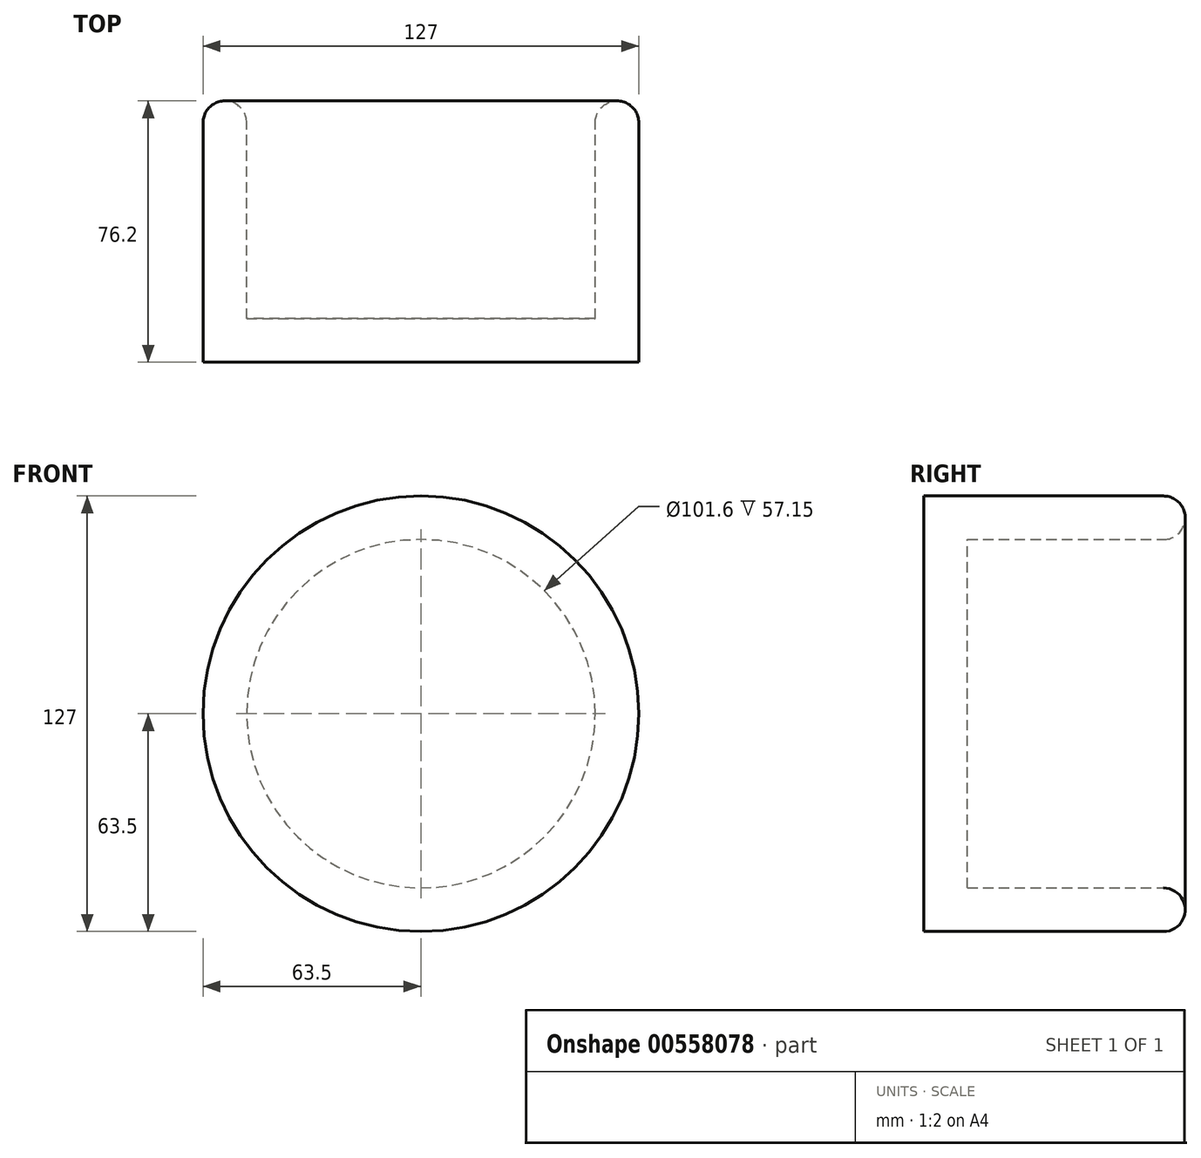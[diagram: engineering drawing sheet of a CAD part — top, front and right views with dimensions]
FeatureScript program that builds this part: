
annotation { "Feature Type Name" : "Feature", "Feature Type Description" : "" }
export const myFeature = defineFeature(function(context is Context, id is Id, definition is map)
    precondition{}
    {
        {
            var Q0;
            Q0=qCreatedBy(makeId("Front.planeOp"),FACE);
            var sketch = newSketch(context, id + "F0", { "sketchPlane" : qUnion([Q0])});
            skCircle(sketch, "E0", {"center": v(0, 0) * mm, "radius": 63.5 * mm});
            skSolve(sketch);
        }
        {
            var Q0;
            Q0=makeQuery(id+"F0.imprint","IMPRINT",FACE,{"disambiguationData":[TD([[makeQuery(id+"F0.imprint","IMPRINT",EDGE,{"derivedFrom":sQuery(id+"F0.wireOp",EDGE,"E0")}),1.0]])]});
            extrude(context, id + "F1", {"entities" : qUnion([Q0]), "depth" : 76.2 * mm, "offsetDistance" : 25.4 * mm});
        }
        {
            var Q0;
            Q0=makeQuery(id+"F1.opExtrude","CAP_FACE",FACE,{"disambiguationData":[OSD([sQuery(id+"F0.wireOp",EDGE,"E0")])],"isStart":true});
            shell(context, id + "F2", {"entities" : qUnion([Q0]), "thickness" : 12.7 * mm});
        }
        {
            var Q0;
            Q0=makeQuery(id+"F1.opExtrude","CAP_EDGE",EDGE,{"disambiguationData":[OSD([sQuery(id+"F0.wireOp",EDGE,"E0")])],"isStart":true});
            var Q1;
            {var subQ0=sQuery(id+"F0.wireOp",EDGE,"E0");Q1=makeQuery(id+"F2.opShell","OFFSET_EDGE",EDGE,{"disambiguationData":[OSD([subQ0]),TDD([makeQuery(id+"F1.opExtrude","CAP_EDGE",EDGE,{"disambiguationData":[OSD([subQ0])],"isStart":true})])]});}
            fillet(context, id + "F3", {"entities" : qUnion([Q0, Q1]), "radius" : 6.35 * mm, "tangentPropagation" : true, "allowEdgeOverflow" : false});
        }
    });
